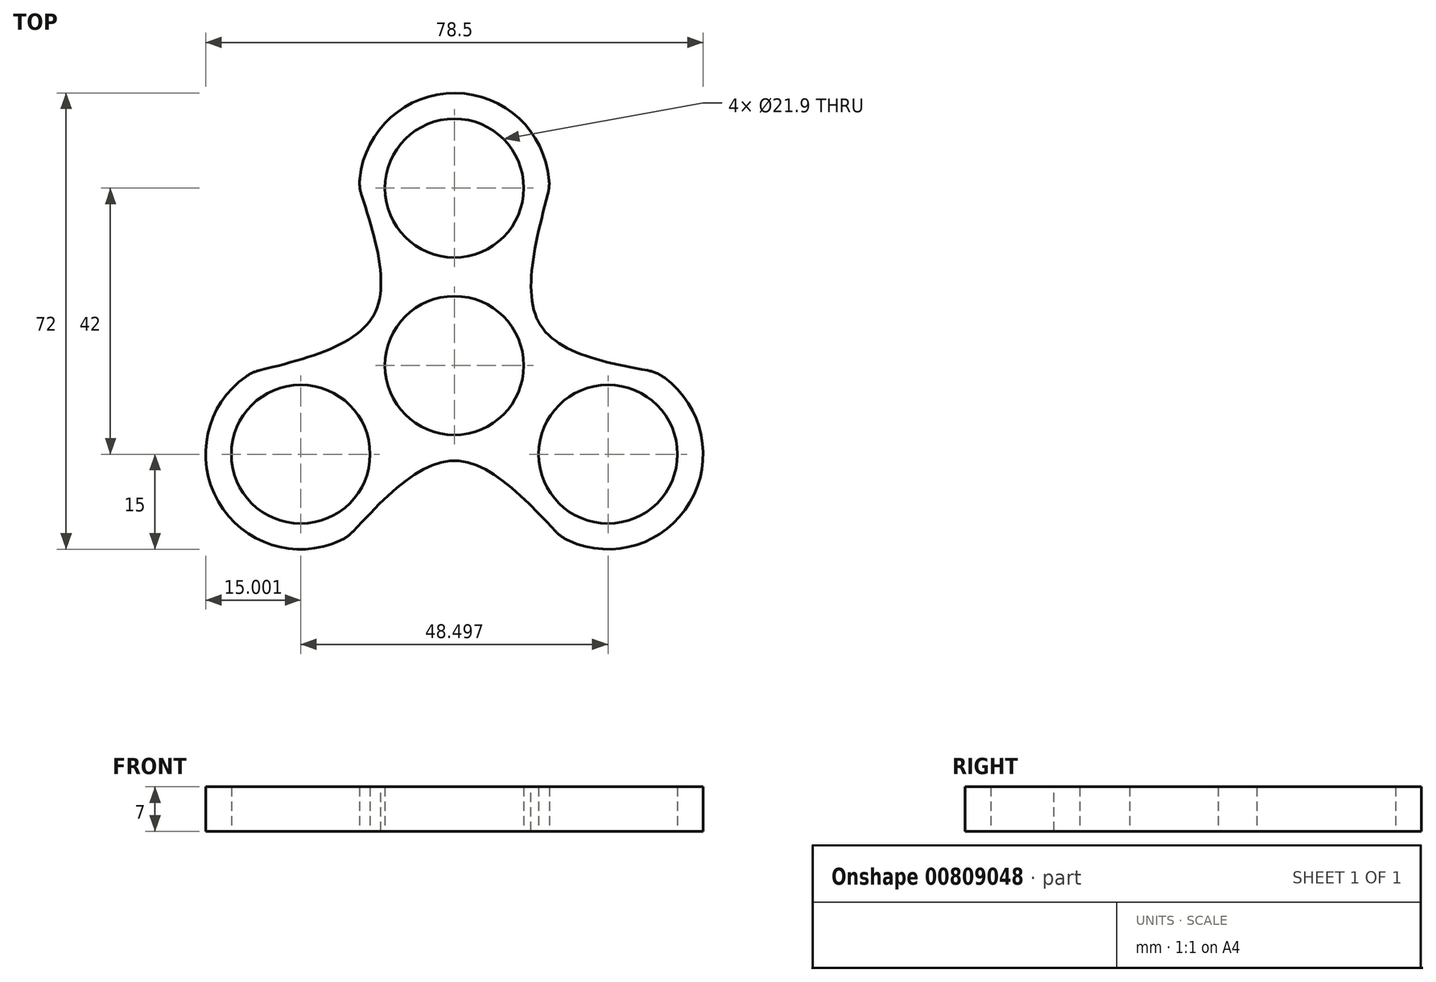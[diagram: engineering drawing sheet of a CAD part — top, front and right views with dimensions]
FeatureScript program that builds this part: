
annotation { "Feature Type Name" : "Feature", "Feature Type Description" : "" }
export const myFeature = defineFeature(function(context is Context, id is Id, definition is map)
    precondition{}
    {
        {
            var Q0;
            Q0=qCreatedBy(makeId("Top.planeOp"),FACE);
            var sketch = newSketch(context, id + "F0", { "sketchPlane" : qUnion([Q0])});
            skCircle(sketch, "E0", {"center": v(0, 0) * mm, "radius": 10.95 * mm});
            skCircle(sketch, "E1", {"center": v(0, 28) * mm, "radius": 10.95 * mm});
            skCircle(sketch, "E2.1.0", {"center": v(-24.25, -14) * mm, "radius": 10.95 * mm});
            skCircle(sketch, "E2.2.0", {"center": v(24.25, -14) * mm, "radius": 10.95 * mm});
            skPoint(sketch, "E3", {"position": v(-15, 28) * mm});
            skPoint(sketch, "E4", {"position": v(15, 28) * mm});
            skLineSegment(sketch, "E5", {"start": v(24.25, -14) * mm, "end": v(0, 0) * mm, "construction": true});
            skPoint(sketch, "E6", {"position": v(9.48, -5.48) * mm});
            skPoint(sketch, "E7.1.0", {"position": v(0, 10.95) * mm});
            skPoint(sketch, "E7.2.0", {"position": v(-9.48, -5.47) * mm});
            skPoint(sketch, "E8.1.0", {"position": v(-31.75, -1) * mm});
            skPoint(sketch, "E8.2.0", {"position": v(16.75, -27) * mm});
            skPoint(sketch, "E9.1.0", {"position": v(-16.75, -27) * mm});
            skPoint(sketch, "E9.2.0", {"position": v(31.75, -1) * mm});
            skFitSpline(sketch, "E10", {"points": [v(-31.75, -1) * mm, v(-12.75, 7.9) * mm, v(-15, 28) * mm], "startDerivative": vector(48.32, 11.85) * mm, "endDerivative": vector(-15.02, 46.28) * mm});
            skFitSpline(sketch, "E11", {"points": [v(15, 28) * mm, v(13.58, 6.38) * mm, v(31.75, -1) * mm], "startDerivative": vector(-13.04, -49.12) * mm, "endDerivative": vector(47.03, -8.57) * mm});
            skFitSpline(sketch, "E12", {"points": [v(16.75, -27) * mm, v(0, -15) * mm, v(-16.75, -27) * mm], "startDerivative": vector(-33.5, 35.97) * mm, "endDerivative": vector(-33.5, -35.97) * mm});
            skArc(sketch, "E13.trimOffspring", {"start": v(14.95, 29.24) * mm, "mid": v(0.13, 43) * mm, "end": v(-14.92, 29.5) * mm});
            skArc(sketch, "E14.trimOffspring", {"start": v(18.02, -27.64) * mm, "mid": v(37.18, -21.6) * mm, "end": v(33.13, -1.91) * mm});
            skArc(sketch, "E15.trimOffspring", {"start": v(-32.9, -1.74) * mm, "mid": v(-37.26, -21.47) * mm, "end": v(-18.02, -27.64) * mm});
            skArc(sketch, "E16.trimOffspring", {"start": v(-12.75, 7.9) * mm, "mid": v(-12.87, 7.7) * mm, "end": v(-12.99, 7.5) * mm});
            skArc(sketch, "E17.trimOffspring", {"start": v(13.58, 6.38) * mm, "mid": v(13.3, 6.94) * mm, "end": v(13, 7.49) * mm});
            skArc(sketch, "E18.filletArc", {"start": v(-14.92, 29.5) * mm, "mid": v(-14.92, 28.2) * mm, "end": v(-14.65, 26.92) * mm});
            skArc(sketch, "E19.filletArc", {"start": v(14.76, 27.1) * mm, "mid": v(14.95, 28.16) * mm, "end": v(14.95, 29.24) * mm});
            skArc(sketch, "E20.filletArc", {"start": v(-30.75, -0.76) * mm, "mid": v(-31.87, -1.15) * mm, "end": v(-32.9, -1.74) * mm});
            skArc(sketch, "E21.filletArc", {"start": v(-18.02, -27.64) * mm, "mid": v(-16.94, -27.02) * mm, "end": v(-16.01, -26.2) * mm});
            skArc(sketch, "E22.filletArc", {"start": v(16.01, -26.2) * mm, "mid": v(16.94, -27.02) * mm, "end": v(18.02, -27.64) * mm});
            skArc(sketch, "E23.filletArc", {"start": v(33.13, -1.91) * mm, "mid": v(31.9, -1.2) * mm, "end": v(30.52, -0.79) * mm});
            skSolve(sketch);
        }
        {
            var Q0;
            Q0=makeQuery(id+"F0.imprint","IMPRINT",FACE,{"disambiguationData":[TD([[makeQuery(id+"F0.imprint","IMPRINT",EDGE,{"derivedFrom":sQuery(id+"F0.wireOp",EDGE,"E0")}),-1.0]])]});
            extrude(context, id + "F1", {"entities" : qUnion([Q0]), "depth" : 7 * mm, "offsetDistance" : 25.4 * mm});
        }
    });
